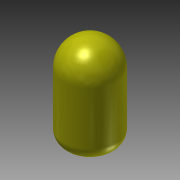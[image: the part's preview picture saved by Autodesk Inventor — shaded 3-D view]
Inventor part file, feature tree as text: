
AUTODESK INVENTOR PART (.ipt)
format: ipt  version: 2015 (Build 190159000, 159)  size: 113,152 bytes
history: native  units: in
note: dims shown in document units (in); Inventor stores cm internally (conversion verified against a paired STEP export)
features: fillet x2, extrude x1
ambient origin geometry x8: Origin, YZ Plane, XZ Plane, XY Plane, X Axis, Y Axis, Z Axis, Center Point
bodies: Solid1 (feature_tree)
feature tree (3):
  extrude  "Extrusion1"  Depth=1.0in
  fillet  "Fillet1"  Radius=1.75in
  fillet  "Fillet2"  Radius=0.5in
